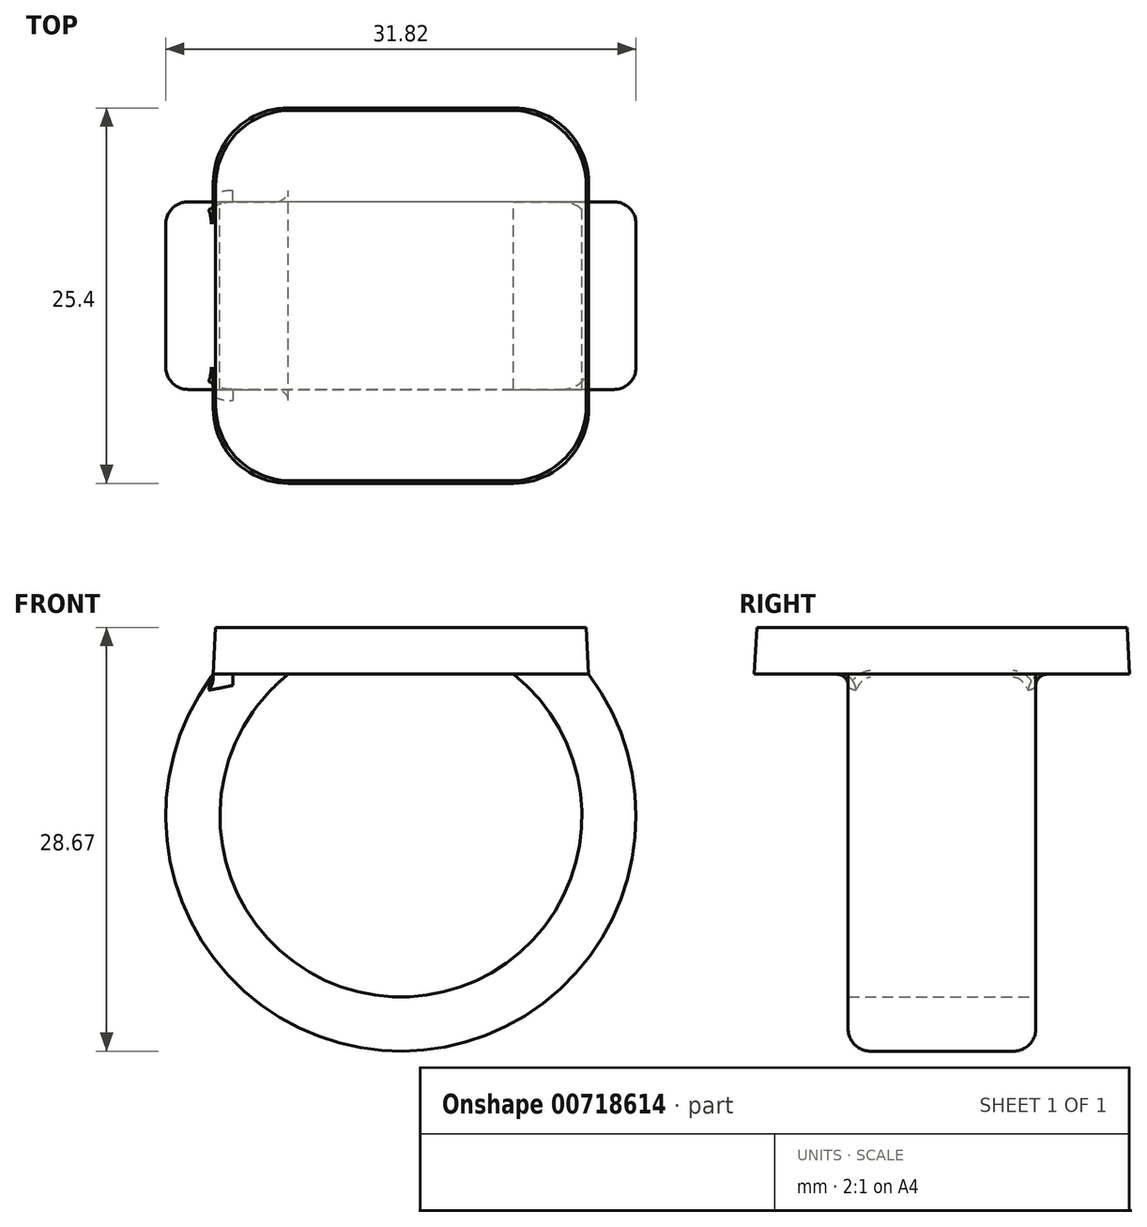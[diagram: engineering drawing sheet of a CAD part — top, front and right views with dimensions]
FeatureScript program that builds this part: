
annotation { "Feature Type Name" : "Feature", "Feature Type Description" : "" }
export const myFeature = defineFeature(function(context is Context, id is Id, definition is map)
    precondition{}
    {
        {
            var Q0;
            Q0=qCreatedBy(makeId("Top.planeOp"),FACE);
            var sketch = newSketch(context, id + "F0", { "sketchPlane" : qUnion([Q0])});
            skLineSegment(sketch, "E0.bottom", {"start": v(-12.7, 12.7) * mm, "end": v(12.7, 12.7) * mm});
            skLineSegment(sketch, "E0.top", {"start": v(-12.7, -12.7) * mm, "end": v(12.7, -12.7) * mm});
            skLineSegment(sketch, "E0.left", {"start": v(-12.7, 12.7) * mm, "end": v(-12.7, -12.7) * mm});
            skLineSegment(sketch, "E0.right", {"start": v(12.7, 12.7) * mm, "end": v(12.7, -12.7) * mm});
            skPoint(sketch, "E0.middle", {"position": v(0, 0) * mm});
            skSolve(sketch);
        }
        {
            var Q0;
            Q0 = qSketchRegion(id + "F0", true);
            extrude(context, id + "F1", {"entities" : qUnion([Q0]), "depth" : 3.17 * mm, "offsetDistance" : 25.4 * mm, "hasDraft" : true, "draftAngle" : 3 * degree, "draftPullDirection" : true});
        }
        {
            var Q0;
            Q0=qCreatedBy(makeId("Front.planeOp"),FACE);
            var sketch = newSketch(context, id + "F2", { "sketchPlane" : qUnion([Q0])});
            skArc(sketch, "E1", {"start": v(-10.16, 0) * mm, "mid": v(0, -23.56) * mm, "end": v(10.16, 0) * mm});
            skSolve(sketch);
        }
        {
            var Q0;
            Q0=makeQuery(id+"F1.opExtrude","CAP_FACE",FACE,{"disambiguationData":[OSD([sQuery(id+"F0.wireOp",EDGE,"E0.bottom"),sQuery(id+"F0.wireOp",EDGE,"E0.top"),sQuery(id+"F0.wireOp",EDGE,"E0.left"),sQuery(id+"F0.wireOp",EDGE,"E0.right")])],"isStart":true});
            var sketch = newSketch(context, id + "F3", { "sketchPlane" : qUnion([Q0])});
            skLineSegment(sketch, "E2.bottom", {"start": v(7.62, 6.35) * mm, "end": v(12.7, 6.35) * mm});
            skLineSegment(sketch, "E2.top", {"start": v(7.62, -6.35) * mm, "end": v(12.7, -6.35) * mm});
            skLineSegment(sketch, "E2.left", {"start": v(7.62, 6.35) * mm, "end": v(7.62, -6.35) * mm});
            skLineSegment(sketch, "E2.right", {"start": v(12.7, 6.35) * mm, "end": v(12.7, -6.35) * mm});
            skPoint(sketch, "E2.middle", {"position": v(10.16, 0) * mm});
            skSolve(sketch);
        }
        {
            var Q0;
            Q0 = qSketchRegion(id + "F3", true);
            var Q1;
            Q1 = qConstructionFilter(qBodyType(qCreatedBy(id + "F2" ,EDGE), BodyType.WIRE), ConstructionObject.NO);
            sweep(context, id + "F4", {"operationType" : NewBodyOperationType.ADD, "profiles" : qUnion([Q0]), "path" : qUnion([Q1])});
        }
        {
            var Q0;
            Q0=qCreatedBy(makeId("Front.planeOp"),FACE);
            var sketch = newSketch(context, id + "F5", { "sketchPlane" : qUnion([Q0])});
            skLineSegment(sketch, "E3.0", {"start": v(-12.7, 0) * mm, "end": v(-10.16, 0) * mm});
            skLineSegment(sketch, "E3.1", {"start": v(-10.16, 0) * mm, "end": v(-10.01, -2.54) * mm});
            skArc(sketch, "E3.2", {"start": v(7.62, 0) * mm, "mid": v(1.74, -21.71) * mm, "end": v(-10.01, -2.54) * mm});
            skPoint(sketch, "E3.3", {"position": v(-10.09, -1.27) * mm});
            skLineSegment(sketch, "E4.trimOffspring", {"start": v(7.62, 0) * mm, "end": v(12.7, 0) * mm});
            skSolve(sketch);
        }
        {
            var Q0;
            Q0=qCreatedBy(makeId("Front.planeOp"),FACE);
            var sketch = newSketch(context, id + "F6", { "sketchPlane" : qUnion([Q0])});
            skLineSegment(sketch, "E5.0.0", {"start": v(12.7, 0) * mm, "end": v(7.62, 0) * mm});
            skLineSegment(sketch, "E5.0.2", {"start": v(7.62, 0) * mm, "end": v(12.7, 0) * mm});
            skLineSegment(sketch, "E5.0.4", {"start": v(-12.7, 0) * mm, "end": v(12.7, 0) * mm});
            skLineSegment(sketch, "E5.0.6", {"start": v(-12.7, 0) * mm, "end": v(12.7, 0) * mm});
            skLineSegment(sketch, "E5.1", {"start": v(-10.16, 0) * mm, "end": v(-10.01, -2.54) * mm});
            skPoint(sketch, "E5.2", {"position": v(-10.01, -2.54) * mm});
            skArc(sketch, "E5.3", {"start": v(7.62, 0) * mm, "mid": v(1.74, -21.71) * mm, "end": v(-10.01, -2.54) * mm});
            skSolve(sketch);
        }
        {
            var Q0;
            Q0=qCreatedBy(makeId("Front.planeOp"),FACE);
            var sketch = newSketch(context, id + "F7", { "sketchPlane" : qUnion([Q0])});
            skLineSegment(sketch, "E6.0", {"start": v(-12.7, 0) * mm, "end": v(12.7, 0) * mm});
            skArc(sketch, "E6.1", {"start": v(7.62, 0) * mm, "mid": v(1.74, -21.71) * mm, "end": v(-10.01, -2.54) * mm});
            skPoint(sketch, "E6.2", {"position": v(-10.09, -1.27) * mm});
            skLineSegment(sketch, "E6.3", {"start": v(-10.16, 0) * mm, "end": v(-10.01, -2.54) * mm});
            skPoint(sketch, "E6.4", {"position": v(0, 0) * mm});
            skPoint(sketch, "E6.5", {"position": v(-10.09, -1.27) * mm});
            skPoint(sketch, "E7.0", {"position": v(-10.01, -2.54) * mm});
            skArc(sketch, "E8.0.0", {"start": v(-7.62, 0) * mm, "mid": v(0, -21.84) * mm, "end": v(7.62, 0) * mm});
            skLineSegment(sketch, "E8.0.1", {"start": v(7.62, 0) * mm, "end": v(-10.16, 0) * mm});
            skSolve(sketch);
        }
        {
            var Q0;
            {var subQ3=sQuery(id+"F7.wireOp",EDGE,"E6.3");Q0=makeQuery(id+"F7.imprint","IMPRINT",FACE,{"disambiguationData":[TD([[makeQuery(id+"F7.imprint","IMPRINT",EDGE,{"derivedFrom":subQ3}),1.0]])]});}
            var Q1;
            Q1=makeQuery(id+"F4.opSweep","SWEPT_FACE",FACE,{"disambiguationData":[OSD([sQuery(id+"F2.wireOp",EDGE,"E1"),sQuery(id+"F3.wireOp",EDGE,"E2.bottom")])]});
            var Q2;
            Q2=makeQuery(id+"F4.opSweep","SWEPT_FACE",FACE,{"disambiguationData":[OSD([sQuery(id+"F2.wireOp",EDGE,"E1"),sQuery(id+"F3.wireOp",EDGE,"E2.top")])]});
            extrude(context, id + "F8", {"entities" : qUnion([Q0]), "operationType" : NewBodyOperationType.ADD, "endBound" : BoundingType.UP_TO_SURFACE, "depth" : 25.4 * mm, "endBoundEntityFace" : qUnion([Q1]), "offsetDistance" : 25.4 * mm, "hasSecondDirection" : true, "secondDirectionBound" : SecondDirectionBoundingType.UP_TO_SURFACE, "secondDirectionOppositeDirection" : true, "secondDirectionDepth" : 25.4 * mm, "secondDirectionBoundEntityFace" : qUnion([Q2])});
        }
        {
            var Q0;
            Q0=makeQuery(id+"F1.opExtrude","SWEPT_EDGE",EDGE,{"disambiguationData":[OSD([sQuery(id+"F0.wireOp",EDGE,"E0.top"),sQuery(id+"F0.wireOp",EDGE,"E0.left")])]});
            var Q1;
            Q1=makeQuery(id+"F1.opExtrude","SWEPT_EDGE",EDGE,{"disambiguationData":[OSD([sQuery(id+"F0.wireOp",EDGE,"E0.top"),sQuery(id+"F0.wireOp",EDGE,"E0.right")])]});
            var Q2;
            Q2=makeQuery(id+"F1.opExtrude","SWEPT_EDGE",EDGE,{"disambiguationData":[OSD([sQuery(id+"F0.wireOp",EDGE,"E0.bottom"),sQuery(id+"F0.wireOp",EDGE,"E0.right")])]});
            var Q3;
            Q3=makeQuery(id+"F1.opExtrude","SWEPT_EDGE",EDGE,{"disambiguationData":[OSD([sQuery(id+"F0.wireOp",EDGE,"E0.bottom"),sQuery(id+"F0.wireOp",EDGE,"E0.left")])]});
            fillet(context, id + "F9", {"entities" : qUnion([Q0, Q1, Q2, Q3]), "radius" : 5.08 * mm, "tangentPropagation" : true, "allowEdgeOverflow" : false});
        }
        {
            var Q0;
            {var subQ0=sQuery(id+"F7.wireOp",EDGE,"E8.0.0");var subQ1=sQuery(id+"F3.wireOp",EDGE,"E2.bottom");var subQ2=sQuery(id+"F2.wireOp",EDGE,"E1");Q0=makeQuery(id+"F8.boolean.opBoolean","MERGE",EDGE,{"derivedFrom":[makeQuery(id+"F4.opSweep","SWEPT_EDGE",EDGE,{"disambiguationData":[OSD([subQ2,subQ1,sQuery(id+"F3.wireOp",EDGE,"E2.left")])]}),makeQuery(id+"F8.opExtrude","TWEAK_EDGE",EDGE,{"derivedFrom":[makeQuery(id+"F4.opSweep","SWEPT_FACE",FACE,{"disambiguationData":[OSD([subQ2,subQ1])]}),makeQuery(id+"F7.imprint","IMPRINT",EDGE,{"disambiguationData":[TD([[makeQuery(id+"F7.imprint","INTERSECT",VERTEX,{"disambiguationData":[OD(0.0)],"derivedFrom":[subQ0,sQuery(id+"F7.wireOp",EDGE,"E8.0.1")]}),-1.0]])],"derivedFrom":subQ0})]})]});}
            var Q1;
            Q1=makeQuery(id+"F4.opSweep","SWEPT_EDGE",EDGE,{"disambiguationData":[OSD([sQuery(id+"F0.wireOp",EDGE,"E0.right"),sQuery(id+"F2.wireOp",EDGE,"E1"),sQuery(id+"F3.wireOp",EDGE,"E2.bottom"),sQuery(id+"F3.wireOp",EDGE,"E2.right")])]});
            var Q2;
            {var subQ0=sQuery(id+"F7.wireOp",EDGE,"E8.0.0");var subQ1=sQuery(id+"F3.wireOp",EDGE,"E2.top");var subQ2=sQuery(id+"F2.wireOp",EDGE,"E1");Q2=makeQuery(id+"F8.boolean.opBoolean","MERGE",EDGE,{"derivedFrom":[makeQuery(id+"F4.opSweep","SWEPT_EDGE",EDGE,{"disambiguationData":[OSD([subQ2,subQ1,sQuery(id+"F3.wireOp",EDGE,"E2.left")])]}),makeQuery(id+"F8.opExtrude","TWEAK_EDGE",EDGE,{"derivedFrom":[makeQuery(id+"F4.opSweep","SWEPT_FACE",FACE,{"disambiguationData":[OSD([subQ2,subQ1])]}),makeQuery(id+"F7.imprint","IMPRINT",EDGE,{"disambiguationData":[TD([[makeQuery(id+"F7.imprint","INTERSECT",VERTEX,{"disambiguationData":[OD(0.0)],"derivedFrom":[subQ0,sQuery(id+"F7.wireOp",EDGE,"E8.0.1")]}),-1.0]])],"derivedFrom":subQ0})]})]});}
            var Q3;
            Q3=makeQuery(id+"F4.opSweep","SWEPT_EDGE",EDGE,{"disambiguationData":[OSD([sQuery(id+"F0.wireOp",EDGE,"E0.right"),sQuery(id+"F2.wireOp",EDGE,"E1"),sQuery(id+"F3.wireOp",EDGE,"E2.top"),sQuery(id+"F3.wireOp",EDGE,"E2.right")])]});
            fillet(context, id + "F10", {"entities" : qUnion([Q0, Q1, Q2, Q3]), "radius" : 1.52 * mm, "tangentPropagation" : true, "allowEdgeOverflow" : false});
        }
        {
            var Q0;
            {var subQ0=sQuery(id+"F0.wireOp",EDGE,"E0.right");Q0=makeQuery(id+"F10.opFillet","BLEND_EDGE",EDGE,{"disambiguationData":[OD(0.0)],"blendedFrom":[makeQuery(id+"F4.opSweep","SWEPT_EDGE",EDGE,{"disambiguationData":[OSD([subQ0,sQuery(id+"F2.wireOp",EDGE,"E1"),sQuery(id+"F3.wireOp",EDGE,"E2.top"),sQuery(id+"F3.wireOp",EDGE,"E2.right")])]}),makeQuery(id+"F1.opExtrude","CAP_FACE",FACE,{"disambiguationData":[OSD([sQuery(id+"F0.wireOp",EDGE,"E0.bottom"),sQuery(id+"F0.wireOp",EDGE,"E0.top"),sQuery(id+"F0.wireOp",EDGE,"E0.left"),subQ0])],"isStart":true})],"blendedInto":[makeQuery(id+"F1.opExtrude","CAP_FACE",FACE,{"disambiguationData":[OSD([sQuery(id+"F0.wireOp",EDGE,"E0.bottom"),sQuery(id+"F0.wireOp",EDGE,"E0.top"),sQuery(id+"F0.wireOp",EDGE,"E0.left"),subQ0])],"isStart":true})]});}
            fillet(context, id + "F11", {"entities" : qUnion([Q0]), "radius" : 0.76 * mm, "tangentPropagation" : true, "allowEdgeOverflow" : false});
        }
    });
